# Revit family: Franke_Unterstellkühleinheit_UC05_EC-A600_MS_EC_A600_FM_EC_A800_FM_EC
name_source: partatom
category: Sonderausstattung
revit_build: Autodesk Revit 2015 (Build: 20140606_1530(x64)
units: mm (PartAtom-declared; Revit-internal decimal feet)

## types (1)
- Unterstellkühleinheit UC05 EC-A600 MS EC,A600 FM EC,A800 FM EC(230V/EU)
    Anzahl der Nullleiter = 1
    Anzahl der Schutzleiter = 1
    Anzahl von Polen = 1
    Aufstellgewicht = 27 kg
    Bauelement = Beistellgerät Unterstellkühleinheit UC05
    Baugruppenkennzeichen = Beistellgerät Unterstellkühleinheit UC05
    Beschreibung = Beistellgerät Unterstellkühleinheit UC05 dient zum Aufbewahren von gekühlter Milch
    Breite = 320 mm  [stored 1.04987 ft]
    Energieverlust nach DIN18873 = 0.380 kWh/24 h - 230 V
    Hersteller = Franke
    Höhe = 264 mm  [stored 0.866142 ft]
    Kosten = 0 $
    Leistung = 90 W
    Milchvorrat = 5 l
    Modell = 410877 - Unterstellkühleinheit UC05 EC - A600 MS EC, A600 FM EC, A800 FM EC
    Netzfrequenz = 50 Hz
    Netzfrequenz alternativ = 60 Hz
    Schallemission = 70 dB
    Sicherung = 10 A
    Spannung = 230 V
    Temperaturbereich = + 3° bis + 8°
    Tiefe = 646 mm  [stored 2.11942 ft]
    URL = http://www.franke.com

note: [stored X ft] marks values corroborated as IEEE doubles in the binary element streams (Revit-internal decimal feet)

## geometry (parser evidence)
native form markers: Extrusion x1
no freeform markers — native parametric forms only
